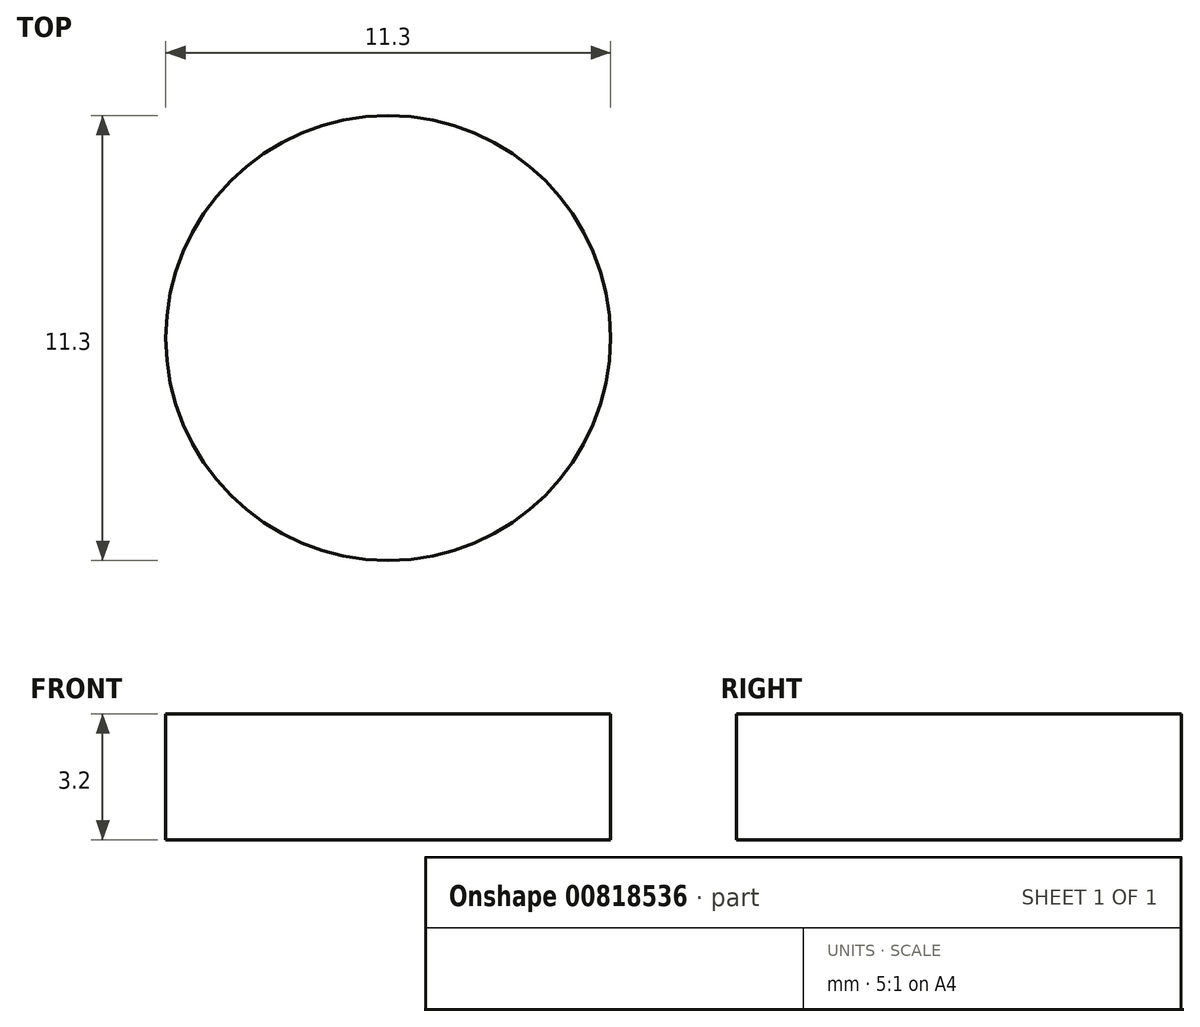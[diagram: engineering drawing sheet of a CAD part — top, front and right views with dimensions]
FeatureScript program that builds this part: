
annotation { "Feature Type Name" : "Feature", "Feature Type Description" : "" }
export const myFeature = defineFeature(function(context is Context, id is Id, definition is map)
    precondition{}
    {
        {
            var Q0;
            Q0=qCreatedBy(makeId("Top.planeOp"),FACE);
            var sketch = newSketch(context, id + "F0", { "sketchPlane" : qUnion([Q0])});
            skCircle(sketch, "E0", {"center": v(0, 0) * mm, "radius": 5.65 * mm});
            skSolve(sketch);
        }
        {
            var Q0;
            Q0 = qSketchRegion(id + "F0", true);
            extrude(context, id + "F1", {"entities" : qUnion([Q0]), "depth" : 3.2 * mm, "offsetDistance" : 25 * mm});
        }
    });
